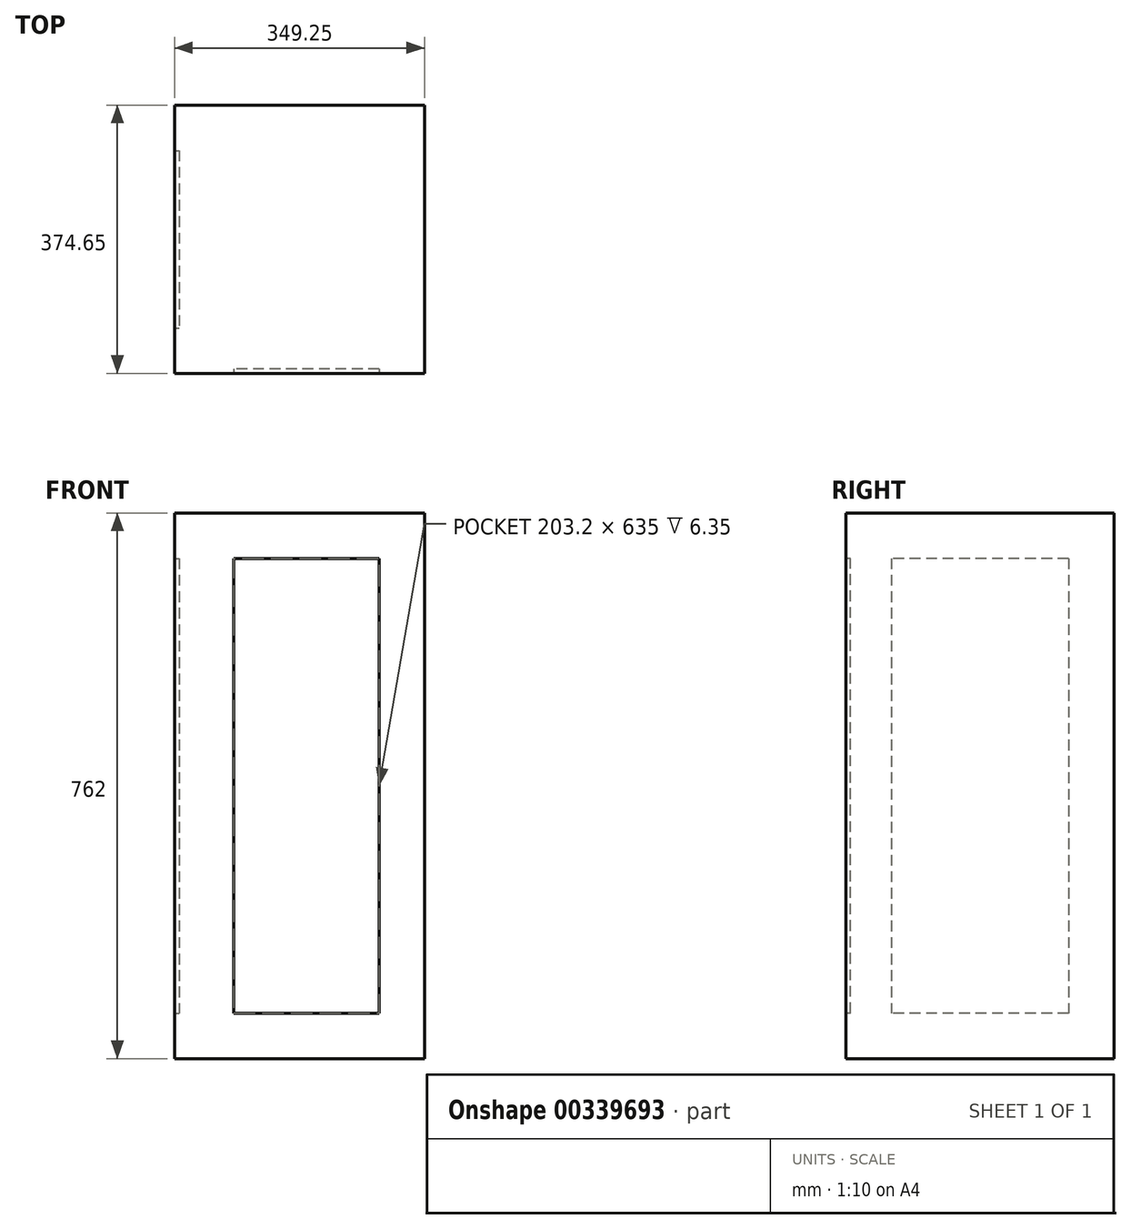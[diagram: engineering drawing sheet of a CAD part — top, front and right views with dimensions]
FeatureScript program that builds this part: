
annotation { "Feature Type Name" : "Feature", "Feature Type Description" : "" }
export const myFeature = defineFeature(function(context is Context, id is Id, definition is map)
    precondition{}
    {
        {
            var Q0;
            Q0=qCreatedBy(makeId("Front.planeOp"),FACE);
            var sketch = newSketch(context, id + "F0", { "sketchPlane" : qUnion([Q0])});
            skLineSegment(sketch, "E0.bottom", {"start": v(213.13, 0) * mm, "end": v(-117.07, 0) * mm});
            skLineSegment(sketch, "E0.top", {"start": v(213.13, 762) * mm, "end": v(-117.07, 762) * mm});
            skLineSegment(sketch, "E0.left", {"start": v(213.13, 0) * mm, "end": v(213.13, 762) * mm});
            skLineSegment(sketch, "E0.right", {"start": v(-117.07, 0) * mm, "end": v(-117.07, 762) * mm});
            skLineSegment(sketch, "E1.0", {"start": v(149.63, 698.5) * mm, "end": v(-53.57, 698.5) * mm});
            skLineSegment(sketch, "E1.1", {"start": v(149.63, 63.5) * mm, "end": v(149.63, 698.5) * mm});
            skLineSegment(sketch, "E1.2", {"start": v(149.63, 63.5) * mm, "end": v(-53.57, 63.5) * mm});
            skLineSegment(sketch, "E1.3", {"start": v(-53.57, 63.5) * mm, "end": v(-53.57, 698.5) * mm});
            skLineSegment(sketch, "E2.bottom", {"start": v(-117.07, 0) * mm, "end": v(263.93, 0) * mm});
            skLineSegment(sketch, "E3.bottom", {"start": v(-117.07, 762) * mm, "end": v(263.93, 762) * mm});
            skSolve(sketch);
        }
        {
            var Q0;
            Q0=makeQuery(id+"F0.imprint","IMPRINT",FACE,{"disambiguationData":[TD([[makeQuery(id+"F0.imprint","IMPRINT",EDGE,{"derivedFrom":sQuery(id+"F0.wireOp",EDGE,"E0.top")}),1.0]])]});
            var Q1;
            Q1=makeQuery(id+"F0.imprint","IMPRINT",FACE,{"disambiguationData":[TD([[makeQuery(id+"F0.imprint","IMPRINT",EDGE,{"derivedFrom":sQuery(id+"F0.wireOp",EDGE,"E1.0")}),1.0]])]});
            var Q2;
            Q2=makeQuery(id+"F0.imprint","IMPRINT",FACE,{"disambiguationData":[TD([[makeQuery(id+"F0.imprint","IMPRINT",EDGE,{"derivedFrom":sQuery(id+"F0.wireOp",EDGE,"E2.bottom")}),-1.0]])]});
            var Q3;
            Q3=makeQuery(id+"F0.imprint","IMPRINT",FACE,{"disambiguationData":[TD([[makeQuery(id+"F0.imprint","IMPRINT",EDGE,{"derivedFrom":sQuery(id+"F0.wireOp",EDGE,"E3.bottom")}),1.0]])]});
            var Q4;
            Q4=makeQuery(id+"F0.imprint","IMPRINT",FACE,{"disambiguationData":[TD([[makeQuery(id+"F0.imprint","IMPRINT",EDGE,{"derivedFrom":sQuery(id+"F0.wireOp",EDGE,"E0.left")}),1.0]])]});
            var Q5;
            Q5=makeQuery(id+"F0.imprint","IMPRINT",FACE,{"disambiguationData":[TD([[makeQuery(id+"F0.imprint","IMPRINT",EDGE,{"derivedFrom":sQuery(id+"F0.wireOp",EDGE,"E3.top")}),-1.0]])]});
            var Q6;
            Q6=makeQuery(id+"F0.imprint","IMPRINT",FACE,{"disambiguationData":[TD([[makeQuery(id+"F0.imprint","IMPRINT",EDGE,{"derivedFrom":sQuery(id+"F0.wireOp",EDGE,"E3.bottom")}),1.0]])]});
            extrude(context, id + "F1", {"entities" : qUnion([Q0, Q1, Q2, Q3, Q4, Q5, Q6]), "oppositeDirection" : true, "depth" : 374.65 * mm, "offsetDistance" : 25.4 * mm});
        }
        {
            var Q0;
            Q0=makeQuery(id+"F0.imprint","IMPRINT",FACE,{"disambiguationData":[TD([[makeQuery(id+"F0.imprint","IMPRINT",EDGE,{"derivedFrom":sQuery(id+"F0.wireOp",EDGE,"E1.0")}),1.0]])]});
            var Q1;
            Q1=makeQuery(id+"F0.imprint","IMPRINT",FACE,{"disambiguationData":[TD([[makeQuery(id+"F0.imprint","IMPRINT",EDGE,{"derivedFrom":sQuery(id+"F0.wireOp",EDGE,"E3.bottom")}),1.0]])]});
            extrude(context, id + "F2", {"entities" : qUnion([Q0, Q1]), "operationType" : NewBodyOperationType.REMOVE, "oppositeDirection" : true, "depth" : 6.35 * mm});
        }
        {
            var Q0;
            Q0=makeQuery(id+"F1.opExtrude","SWEPT_FACE",FACE,{"disambiguationData":[OSD([sQuery(id+"F0.wireOp",EDGE,"E0.right")])]});
            var sketch = newSketch(context, id + "F3", { "sketchPlane" : qUnion([Q0])});
            skLineSegment(sketch, "E4.bottom", {"start": v(-374.65, 762) * mm, "end": v(0, 762) * mm});
            skLineSegment(sketch, "E4.top", {"start": v(-374.65, 0) * mm, "end": v(0, 0) * mm});
            skLineSegment(sketch, "E4.left", {"start": v(-374.65, 762) * mm, "end": v(-374.65, 0) * mm});
            skLineSegment(sketch, "E4.right", {"start": v(0, 762) * mm, "end": v(0, 0) * mm});
            skLineSegment(sketch, "E5.0", {"start": v(-311.15, 698.5) * mm, "end": v(-63.5, 698.5) * mm});
            skLineSegment(sketch, "E5.1", {"start": v(-311.15, 698.5) * mm, "end": v(-311.15, 63.5) * mm});
            skLineSegment(sketch, "E5.2", {"start": v(-311.15, 63.5) * mm, "end": v(-63.5, 63.5) * mm});
            skLineSegment(sketch, "E5.3", {"start": v(-63.5, 698.5) * mm, "end": v(-63.5, 63.5) * mm});
            skSolve(sketch);
        }
        {
            var Q0;
            Q0=makeQuery(id+"F3.imprint","IMPRINT",FACE,{"disambiguationData":[TD([[makeQuery(id+"F3.imprint","IMPRINT",EDGE,{"derivedFrom":sQuery(id+"F3.wireOp",EDGE,"E4.bottom")}),-1.0]])]});
            extrude(context, id + "F4", {"entities" : qUnion([Q0]), "operationType" : NewBodyOperationType.ADD, "depth" : 19.05 * mm, "offsetDistance" : 25.4 * mm});
        }
        {
            var Q0;
            Q0=makeQuery(id+"F1.opExtrude","SWEPT_FACE",FACE,{"disambiguationData":[OSD([sQuery(id+"F0.wireOp",EDGE,"E0.right")])]});
            extrude(context, id + "F5", {"entities" : qUnion([Q0]), "operationType" : NewBodyOperationType.ADD, "depth" : 12.7 * mm, "offsetDistance" : 25.4 * mm});
        }
    });
